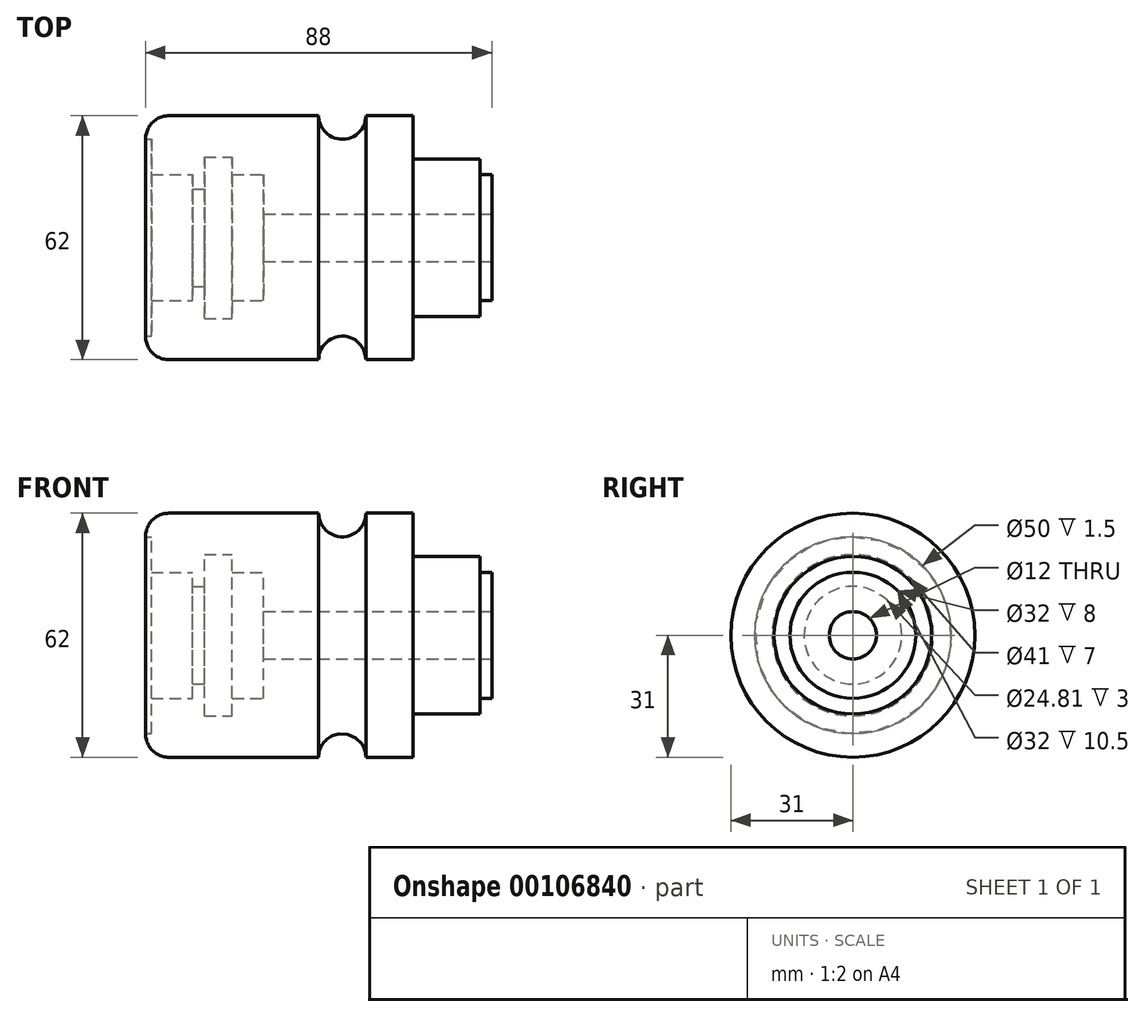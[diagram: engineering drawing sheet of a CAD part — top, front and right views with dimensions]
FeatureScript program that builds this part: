
annotation { "Feature Type Name" : "Feature", "Feature Type Description" : "" }
export const myFeature = defineFeature(function(context is Context, id is Id, definition is map)
    precondition{}
    {
        {
            var Q0;
            Q0=qCreatedBy(makeId("Front.planeOp"),FACE);
            var sketch = newSketch(context, id + "F0", { "sketchPlane" : qUnion([Q0])});
            skLineSegment(sketch, "E0", {"start": v(0, 0) * mm, "end": v(89, 0) * mm, "construction": true});
            skLineSegment(sketch, "E1", {"start": v(0, 0) * mm, "end": v(0, 25) * mm});
            skLineSegment(sketch, "E2", {"start": v(6, 31) * mm, "end": v(44, 31) * mm});
            skArc(sketch, "E3", {"start": v(44, 31) * mm, "mid": v(50, 25) * mm, "end": v(56, 31) * mm});
            skLineSegment(sketch, "E4", {"start": v(56, 31) * mm, "end": v(68, 31) * mm});
            skLineSegment(sketch, "E5", {"start": v(68, 31) * mm, "end": v(68, 20) * mm});
            skLineSegment(sketch, "E6", {"start": v(68, 20) * mm, "end": v(85, 20) * mm});
            skLineSegment(sketch, "E7", {"start": v(85, 20) * mm, "end": v(85, 16) * mm});
            skLineSegment(sketch, "E8", {"start": v(85, 16) * mm, "end": v(88, 16) * mm});
            skLineSegment(sketch, "E9", {"start": v(88, 16) * mm, "end": v(88, 0) * mm});
            skLineSegment(sketch, "E10", {"start": v(56, 31) * mm, "end": v(56, 0) * mm});
            skLineSegment(sketch, "E11", {"start": v(44, 31) * mm, "end": v(44, 0) * mm});
            skLineSegment(sketch, "E12", {"start": v(68, 20) * mm, "end": v(68, 0) * mm});
            skLineSegment(sketch, "E13", {"start": v(85, 16) * mm, "end": v(85, 0) * mm});
            skLineSegment(sketch, "E14", {"start": v(0, 0) * mm, "end": v(88, 0) * mm});
            skPoint(sketch, "E15.visualSharp", {"position": v(0, 31) * mm});
            skArc(sketch, "E15.filletArc", {"start": v(6, 31) * mm, "mid": v(1.76, 29.24) * mm, "end": v(0, 25) * mm});
            skSolve(sketch);
        }
        {
            var Q0;
            Q0 = qSketchRegion(id + "F0", true);
            var Q1;
            Q1=sQuery(id+"F0.wireOp",EDGE,"E14");
            revolve(context, id + "F1", {"entities" : qUnion([Q0]), "axis" : qUnion([Q1]), "revolveType" : RevolveType.FULL});
        }
        {
            var Q0;
            Q0=qCreatedBy(makeId("Front.planeOp"),FACE);
            var sketch = newSketch(context, id + "F2", { "sketchPlane" : qUnion([Q0])});
            skLineSegment(sketch, "E16", {"start": v(0, 0) * mm, "end": v(0, 25) * mm});
            skLineSegment(sketch, "E17", {"start": v(0, 25) * mm, "end": v(1.5, 25) * mm});
            skLineSegment(sketch, "E18", {"start": v(1.5, 25) * mm, "end": v(1.5, 16) * mm});
            skLineSegment(sketch, "E19", {"start": v(1.5, 16) * mm, "end": v(12, 16) * mm});
            skLineSegment(sketch, "E20", {"start": v(12, 16) * mm, "end": v(12, 12.4) * mm});
            skLineSegment(sketch, "E21", {"start": v(12, 12.4) * mm, "end": v(15, 12.4) * mm});
            skLineSegment(sketch, "E22", {"start": v(15, 12.4) * mm, "end": v(15, 20.5) * mm});
            skLineSegment(sketch, "E23", {"start": v(15, 20.5) * mm, "end": v(22, 20.5) * mm});
            skLineSegment(sketch, "E24", {"start": v(22, 20.5) * mm, "end": v(22, 16) * mm});
            skLineSegment(sketch, "E25", {"start": v(22, 16) * mm, "end": v(30, 16) * mm});
            skLineSegment(sketch, "E26", {"start": v(30, 16) * mm, "end": v(30, 6) * mm});
            skLineSegment(sketch, "E27", {"start": v(30, 6) * mm, "end": v(88, 6) * mm});
            skLineSegment(sketch, "E28", {"start": v(0, 0) * mm, "end": v(88, 0) * mm});
            skLineSegment(sketch, "E29", {"start": v(88, 6) * mm, "end": v(88, 0) * mm});
            skLineSegment(sketch, "E30", {"start": v(1.5, 16) * mm, "end": v(1.5, 0) * mm});
            skLineSegment(sketch, "E31", {"start": v(12, 12.4) * mm, "end": v(12, 0) * mm});
            skLineSegment(sketch, "E32", {"start": v(15, 12.4) * mm, "end": v(15, 0) * mm});
            skLineSegment(sketch, "E33", {"start": v(22, 16) * mm, "end": v(22, 0) * mm});
            skLineSegment(sketch, "E34", {"start": v(30, 6) * mm, "end": v(30, 0) * mm});
            skLineSegment(sketch, "E35", {"start": v(30, 0) * mm, "end": v(30, 0) * mm});
            skSolve(sketch);
        }
        {
            var Q0;
            Q0 = qSketchRegion(id + "F2", true);
            var Q1;
            Q1=sQuery(id+"F2.wireOp",EDGE,"E28");
            revolve(context, id + "F3", {"operationType" : NewBodyOperationType.REMOVE, "entities" : qUnion([Q0]), "axis" : qUnion([Q1]), "revolveType" : RevolveType.FULL, "oppositeDirection" : true});
        }
    });
